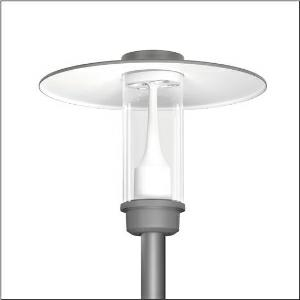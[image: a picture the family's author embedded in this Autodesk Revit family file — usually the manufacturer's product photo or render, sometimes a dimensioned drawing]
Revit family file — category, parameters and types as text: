
# Revit family: litepole_2_iq___pl1_2s_5xa5425rf14h_b6f1
name_source: partatom
category: Lighting Fixtures
units: mm (PartAtom-declared; Revit-internal decimal feet)

## family parameters
Cut with Voids When Loaded = No
Host = Face
Light Source = No
Part Type = Normal
Room Calculation Point = No
Round Connector Dimension = Use Diameter
Shared = No

## types (1)
- --- (1 x LED, 2990 lm, 18.5 W, 4000K)
    Apparent Load = 19 VA
    CIE Flux Codes = 22 60 92 98 100
    Color Rendering = 70
    Color Temperature = 4000K
    Default Elevation = 1800 mm
    Description = Litepole 2 iQ, mast luminaire, Module 540 iQ-SR, primary light control with 3 zone facetted reflector, of plastic, silver coated, highly specular, structured, primary optical cover: cover, of PMMA, transparent, light distribution: PL1.2s, light emission: direct distribution, primary light characteristic: symmetric, installation type: post-top, LED, High Power LED, rated luminous flux: 2.990lm, luminous efficacy: 162lm/W, light colour: 740, colour temperature: 4000K, control gear: iQ Street-Remote, control: pre-setting: logarithmic dimming characteristic, Street-Remote, Auto-Match, Temp-Guard, Lumen-Switch, Night-Set, Smart-Wire, Light-Fading, Desk-Remote (wireless, voltage-free reading and setting of iQ features in the workshop via application-optimized NFC function/RFID function), optimised constant luminous flux control (CLO 2.0), with terminal, 6-pole, max. 2.5mm², mains connection: 230..240V, AC, 50/60Hz, start of lifetime: 19W, end of service life: 20W, reduction: 10W, luminaire housing, upper part, of aluminium, coated, Siteco® metallic grey (DB 702S), diameter: 750mm, height: 590mm, spigot size: d x l = 76 x 70mm (post-top) | with reducer (optional accessory) 60 x 70mm, mounting height: 3..5m, post-top mast mounting element, of diecast aluminium, coated, Siteco® metallic grey (DB 702S), Module 540 iQ-SR, traffic white (RAL 9016), equipment: standard, protection rating (complete): IP65, insulation class (complete): insulation class II (safety insulation), certification: CE, ENEC, VDE, packaging unit: 1 piece

Light Distribution: PL1.2s
    Height = 590 mm
    Lamp = 1 x LED
    Lamp Light Flux = 2990 lm
    Lamp Power = 18.5 W
    Lamp count = 1
    Length = 750 mm
    Luminous efficacy = 162 lm/W
    Manufacturer = Siteco
    ModVariant = No
    Model = 5XA5425RF14H
    Number of Poles = 1
    OnlyDefault = Yes
    Power Factor = 1
    Product Name = Litepole 2 iQ | PL1.2s
    Product group = mast luminaire | pylon top
    ProductGroupID = 6100
    Protection Class = Protection class II
    Protection Degree = IP 65
    RLX_Detail_Level = 1
    RLX_Emergency_Light_Flux = 0 lm
    RLX_Emergency_Type = 0
    RLX_Emergency_Type_DB = No
    RlxData = <blob elided: 29449 chars, md5=00133227>
    Socket = socket
    Standby Power = 0 W
    System Light Flux = 2990 lm
    System Power = 19 W
    Type Comments = factory setting: luminous flux: 100 % | dim-lin: 254 | 385 mA
    Type Image = l_1006518.jpg
    URL = http://relux.com
    VarID = @adj_144610
    Voltage = 0 V
    Weight = 0.00 kg
    Width = 0 mm  [stored 0 ft]

note: [stored X ft] marks values corroborated as IEEE doubles in the binary element streams (Revit-internal decimal feet)

## geometry (parser evidence)
native form markers: Blend x4, Sweep x11
no freeform markers — native parametric forms only
